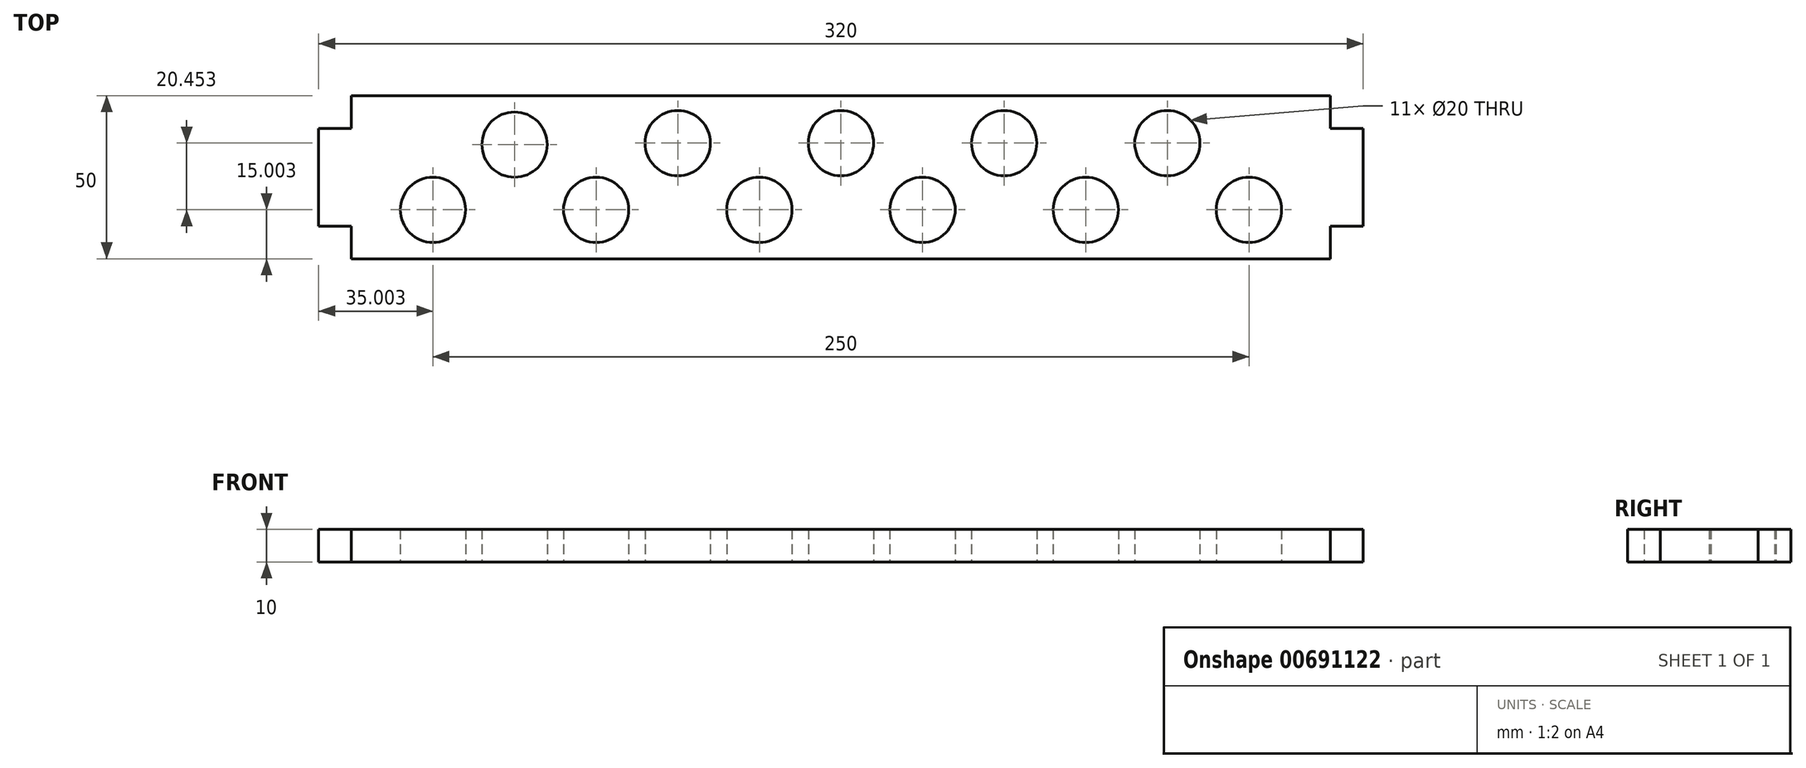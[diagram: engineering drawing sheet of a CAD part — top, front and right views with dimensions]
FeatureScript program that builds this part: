
annotation { "Feature Type Name" : "Feature", "Feature Type Description" : "" }
export const myFeature = defineFeature(function(context is Context, id is Id, definition is map)
    precondition{}
    {
        {
            var Q0;
            Q0=qCreatedBy(makeId("Top.planeOp"),FACE);
            var sketch = newSketch(context, id + "F0", { "sketchPlane" : qUnion([Q0])});
            skLineSegment(sketch, "E0.bottom", {"start": v(54.8, 22.82) * mm, "end": v(-245.2, 22.82) * mm});
            skLineSegment(sketch, "E0.top", {"start": v(54.8, 72.82) * mm, "end": v(-245.2, 72.82) * mm});
            skLineSegment(sketch, "E0.left", {"start": v(64.8, 32.82) * mm, "end": v(64.8, 62.82) * mm});
            skLineSegment(sketch, "E0.right", {"start": v(-255.2, 32.82) * mm, "end": v(-255.2, 62.82) * mm});
            skLineSegment(sketch, "E1", {"start": v(-245.2, 72.82) * mm, "end": v(-245.2, 22.82) * mm});
            skLineSegment(sketch, "E2", {"start": v(54.8, 72.82) * mm, "end": v(54.8, 22.82) * mm});
            skCircle(sketch, "E3", {"center": v(-220.2, 37.82) * mm, "radius": 10 * mm});
            skLineSegment(sketch, "E4", {"start": v(54.8, 62.82) * mm, "end": v(64.8, 62.82) * mm});
            skLineSegment(sketch, "E5", {"start": v(54.8, 32.82) * mm, "end": v(64.8, 32.82) * mm});
            skLineSegment(sketch, "E6.MirrorCS", {"start": v(-245.2, 62.82) * mm, "end": v(-255.2, 62.82) * mm});
            skLineSegment(sketch, "E7.MirrorCS", {"start": v(-245.2, 32.82) * mm, "end": v(-255.2, 32.82) * mm});
            skLineSegment(sketch, "E8", {"start": v(54.8, 62.82) * mm, "end": v(54.8, 72.82) * mm});
            skLineSegment(sketch, "E9", {"start": v(54.8, 22.82) * mm, "end": v(54.8, 32.82) * mm});
            skLineSegment(sketch, "E10", {"start": v(-245.2, 72.82) * mm, "end": v(-245.2, 62.82) * mm});
            skPoint(sketch, "E11.orphan", {"position": v(64.8, 72.82) * mm});
            skPoint(sketch, "E12.orphan", {"position": v(64.8, 22.82) * mm});
            skPoint(sketch, "E13.orphan", {"position": v(-255.2, 72.82) * mm});
            skPoint(sketch, "E14.start.orphan", {"position": v(-255.2, 22.82) * mm});
            skCircle(sketch, "E15", {"center": v(-195.2, 57.82) * mm, "radius": 10 * mm});
            skCircle(sketch, "E16", {"center": v(-170.2, 37.82) * mm, "radius": 10 * mm});
            skCircle(sketch, "E17", {"center": v(-145.2, 58.28) * mm, "radius": 10 * mm});
            skCircle(sketch, "E18", {"center": v(-120.2, 37.82) * mm, "radius": 10 * mm});
            skCircle(sketch, "E19", {"center": v(-95.2, 58.28) * mm, "radius": 10 * mm});
            skCircle(sketch, "E20", {"center": v(-70.2, 37.82) * mm, "radius": 10 * mm});
            skCircle(sketch, "E21", {"center": v(-45.2, 58.28) * mm, "radius": 10 * mm});
            skCircle(sketch, "E22", {"center": v(-20.2, 37.82) * mm, "radius": 10 * mm});
            skCircle(sketch, "E23", {"center": v(4.8, 58.28) * mm, "radius": 10 * mm});
            skCircle(sketch, "E24", {"center": v(29.8, 37.82) * mm, "radius": 10 * mm});
            skSolve(sketch);
        }
        {
            var Q0;
            {var subQ3=sQuery(id+"F0.wireOp",EDGE,"E0.bottom");Q0=makeQuery(id+"F0.imprint","IMPRINT",FACE,{"disambiguationData":[TD([[makeQuery(id+"F0.imprint","IMPRINT",EDGE,{"derivedFrom":subQ3}),-1.0]])]});}
            var Q1;
            Q1=makeQuery(id+"F0.imprint","IMPRINT",FACE,{"disambiguationData":[TD([[makeQuery(id+"F0.imprint","IMPRINT",EDGE,{"derivedFrom":sQuery(id+"F0.wireOp",EDGE,"E0.right")}),-1.0]])]});
            var Q2;
            Q2=makeQuery(id+"F0.imprint","IMPRINT",FACE,{"disambiguationData":[TD([[makeQuery(id+"F0.imprint","IMPRINT",EDGE,{"derivedFrom":sQuery(id+"F0.wireOp",EDGE,"E0.left")}),1.0]])]});
            extrude(context, id + "F1", {"entities" : qUnion([Q0, Q1, Q2]), "depth" : 10 * mm, "offsetDistance" : 25 * mm});
        }
    });
